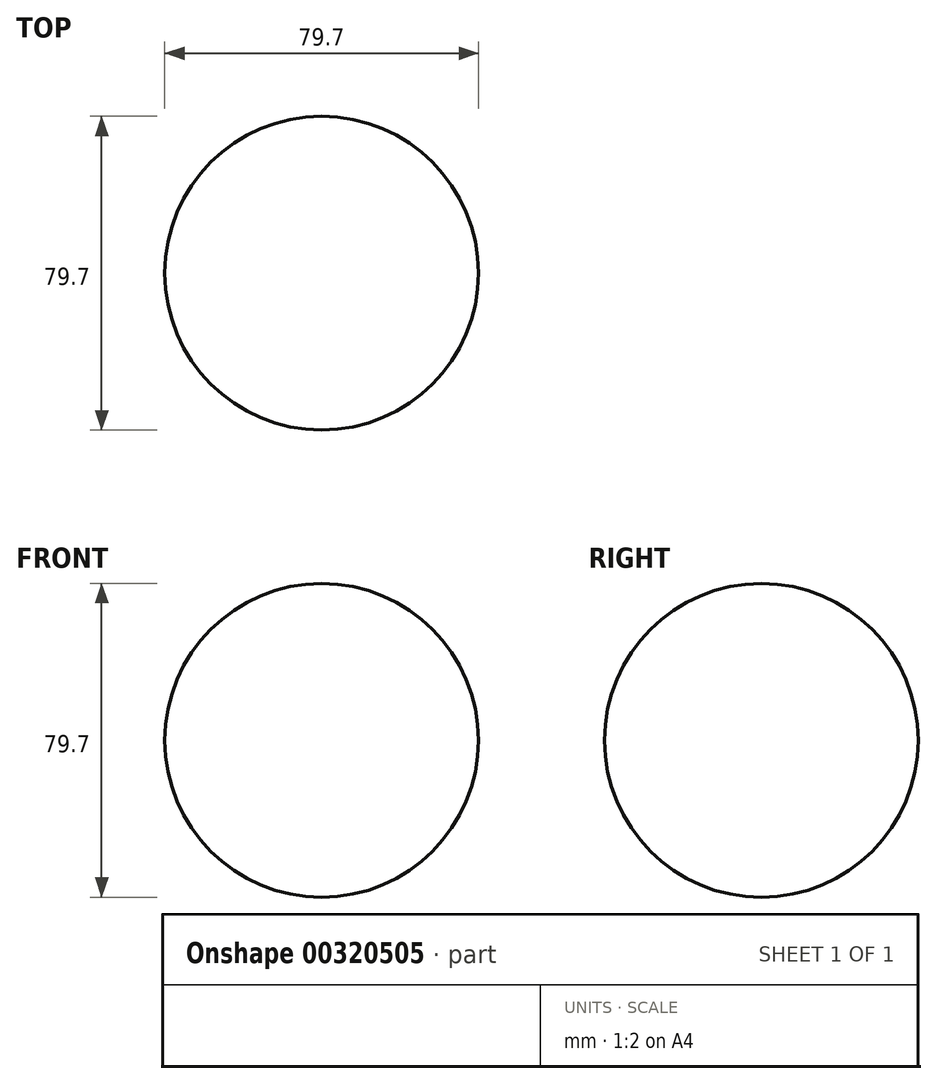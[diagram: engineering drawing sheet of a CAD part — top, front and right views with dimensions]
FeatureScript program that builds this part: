
annotation { "Feature Type Name" : "Feature", "Feature Type Description" : "" }
export const myFeature = defineFeature(function(context is Context, id is Id, definition is map)
    precondition{}
    {
        {
            var Q0;
            Q0=qCreatedBy(makeId("Front.planeOp"),FACE);
            var sketch = newSketch(context, id + "F0", { "sketchPlane" : qUnion([Q0])});
            skLineSegment(sketch, "E0", {"start": v(0, 76.48) * mm, "end": v(0, -76.95) * mm, "construction": true});
            skArc(sketch, "E1", {"start": v(0, 39.85) * mm, "mid": v(-39.85, 0) * mm, "end": v(0, -39.85) * mm});
            skLineSegment(sketch, "E2", {"start": v(0, -39.85) * mm, "end": v(0, 39.85) * mm});
            skSolve(sketch);
        }
        {
            var Q0;
            Q0=makeQuery(id+"F0.imprint","IMPRINT",FACE,{"disambiguationData":[TD([[makeQuery(id+"F0.imprint","IMPRINT",EDGE,{"derivedFrom":sQuery(id+"F0.wireOp",EDGE,"E1")}),1.0]])]});
            var Q1;
            Q1=sQuery(id+"F0.wireOp",EDGE,"E0");
            revolve(context, id + "F1", {"entities" : qUnion([Q0]), "axis" : qUnion([Q1]), "revolveType" : RevolveType.FULL});
        }
    });
